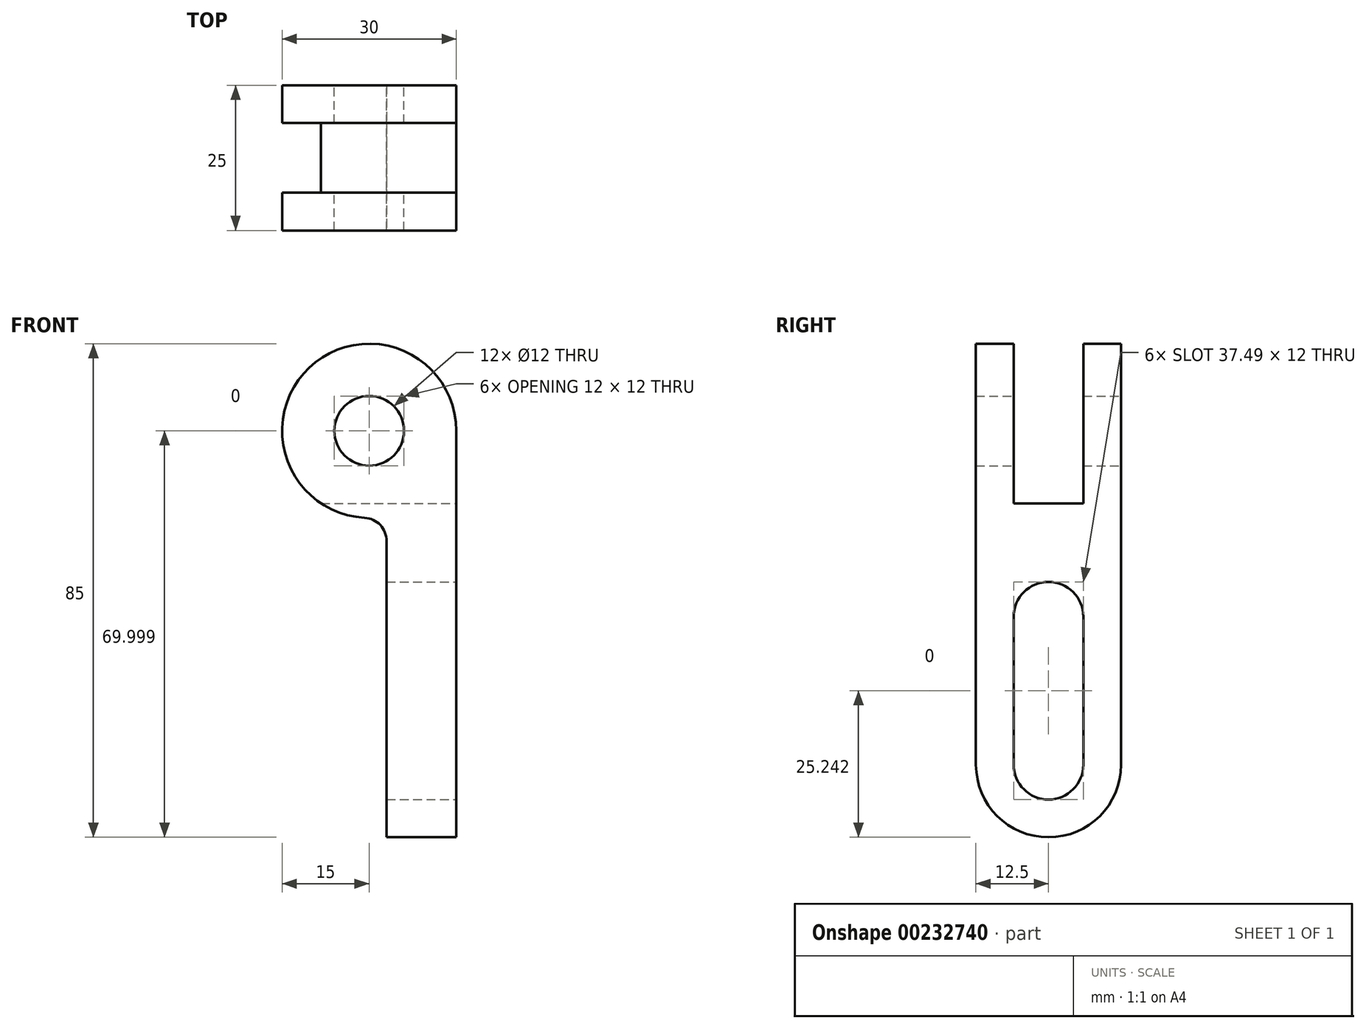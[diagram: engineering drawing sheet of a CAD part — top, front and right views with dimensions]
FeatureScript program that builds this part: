
annotation { "Feature Type Name" : "Feature", "Feature Type Description" : "" }
export const myFeature = defineFeature(function(context is Context, id is Id, definition is map)
    precondition{}
    {
        {
            var Q0;
            Q0=qCreatedBy(makeId("Front.planeOp"),FACE);
            var sketch = newSketch(context, id + "F0", { "sketchPlane" : qUnion([Q0])});
            skCircle(sketch, "E0", {"center": v(-31.82, 39.8) * mm, "radius": 6 * mm});
            skArc(sketch, "E1", {"start": v(-16.82, 39.8) * mm, "mid": v(-42.14, 50.7) * mm, "end": v(-32.6, 24.83) * mm});
            skLineSegment(sketch, "E2", {"start": v(-6.57, 39.8) * mm, "end": v(-62.09, 39.8) * mm, "construction": true});
            skLineSegment(sketch, "E3", {"start": v(-16.82, 39.8) * mm, "end": v(-16.82, -30.2) * mm});
            skLineSegment(sketch, "E4", {"start": v(-16.82, -30.2) * mm, "end": v(-28.82, -30.2) * mm});
            skLineSegment(sketch, "E5", {"start": v(-28.82, -30.2) * mm, "end": v(-28.82, 20.84) * mm});
            skArc(sketch, "E6", {"start": v(-28.82, 20.84) * mm, "mid": v(-29.92, 23.59) * mm, "end": v(-32.6, 24.83) * mm});
            skSolve(sketch);
        }
        {
            var Q0;
            Q0=makeQuery(id+"F0.imprint","IMPRINT",FACE,{"disambiguationData":[TD([[makeQuery(id+"F0.imprint","IMPRINT",EDGE,{"derivedFrom":sQuery(id+"F0.wireOp",EDGE,"E0")}),-1.0]])]});
            extrude(context, id + "F1", {"entities" : qUnion([Q0]), "depth" : 25 * mm});
        }
        {
            var Q0;
            Q0=qCreatedBy(makeId("Right.planeOp"),FACE);
            var sketch = newSketch(context, id + "F2", { "sketchPlane" : qUnion([Q0])});
            skLineSegment(sketch, "E7.0.1", {"start": v(0, -30.2) * mm, "end": v(-25, -30.2) * mm});
            skLineSegment(sketch, "E7.0.3", {"start": v(-25, 20.84) * mm, "end": v(0, 20.84) * mm});
            skLineSegment(sketch, "E8.0", {"start": v(-25, 24.83) * mm, "end": v(0, 24.83) * mm});
            skLineSegment(sketch, "E9", {"start": v(-46.82, 54.8) * mm, "end": v(-46.82, 54.8) * mm});
            skLineSegment(sketch, "E10.0", {"start": v(-25, -30.2) * mm, "end": v(0, -30.2) * mm});
            skLineSegment(sketch, "E10.1", {"start": v(0, 24.83) * mm, "end": v(0, 24.83) * mm});
            skLineSegment(sketch, "E10.2", {"start": v(-25, 24.83) * mm, "end": v(-25, 24.83) * mm});
            skLineSegment(sketch, "E10.4", {"start": v(0, 20.84) * mm, "end": v(0, 24.83) * mm});
            skLineSegment(sketch, "E10.7", {"start": v(0, 33.8) * mm, "end": v(0, 45.8) * mm});
            skLineSegment(sketch, "E10.8", {"start": v(-25, 33.8) * mm, "end": v(-25, 45.8) * mm});
            skLineSegment(sketch, "E10.10", {"start": v(-25, 20.84) * mm, "end": v(-25, 24.83) * mm});
            skLineSegment(sketch, "E10.11", {"start": v(-25, -30.2) * mm, "end": v(0, -30.2) * mm});
            skLineSegment(sketch, "E10.12", {"start": v(-16.82, 39.8) * mm, "end": v(-16.82, 39.8) * mm});
            skLineSegment(sketch, "E10.15", {"start": v(0, -30.2) * mm, "end": v(0, -30.2) * mm});
            skLineSegment(sketch, "E10.16", {"start": v(-25, -30.2) * mm, "end": v(-25, -30.2) * mm});
            skLineSegment(sketch, "E11", {"start": v(-25, 54.8) * mm, "end": v(0, 54.8) * mm});
            skLineSegment(sketch, "E12.0.0", {"start": v(0, 20.84) * mm, "end": v(0, -30.2) * mm});
            skLineSegment(sketch, "E12.0.2", {"start": v(-25, -30.2) * mm, "end": v(-25, 20.84) * mm});
            skArc(sketch, "E13", {"start": v(-25, -17.7) * mm, "mid": v(-12.5, -30.2) * mm, "end": v(0, -17.7) * mm});
            skArc(sketch, "E14", {"start": v(-18.5, -17.7) * mm, "mid": v(-12.5, -23.7) * mm, "end": v(-6.5, -17.7) * mm});
            skArc(sketch, "E15", {"start": v(-6.5, 7.8) * mm, "mid": v(-12.5, 13.8) * mm, "end": v(-18.5, 7.8) * mm});
            skLineSegment(sketch, "E16", {"start": v(-12.5, -36.92) * mm, "end": v(-12.5, -23.7) * mm});
            skPoint(sketch, "E16.endSnap0", {"position": v(-12.5, 24.83) * mm});
            skLineSegment(sketch, "E17", {"start": v(-18.5, 7.8) * mm, "end": v(-18.5, -17.7) * mm});
            skLineSegment(sketch, "E18", {"start": v(-6.5, 7.8) * mm, "end": v(-6.5, -17.7) * mm});
            skLineSegment(sketch, "E19.trimOffspring", {"start": v(-12.5, 13.8) * mm, "end": v(-12.5, 65.83) * mm});
            skLineSegment(sketch, "E20.bottom", {"start": v(-6.5, 27.3) * mm, "end": v(-18.5, 27.3) * mm});
            skLineSegment(sketch, "E20.top", {"start": v(-6.5, 82.3) * mm, "end": v(-18.5, 82.3) * mm});
            skLineSegment(sketch, "E20.left", {"start": v(-6.5, 27.3) * mm, "end": v(-6.5, 82.3) * mm});
            skLineSegment(sketch, "E20.right", {"start": v(-18.5, 27.3) * mm, "end": v(-18.5, 82.3) * mm});
            skPoint(sketch, "E20.middle", {"position": v(-12.5, 54.8) * mm});
            skLineSegment(sketch, "E21", {"start": v(-25, 54.8) * mm, "end": v(-25, 24.83) * mm});
            skLineSegment(sketch, "E22", {"start": v(0, 54.8) * mm, "end": v(0, 24.83) * mm});
            skSolve(sketch);
        }
        {
            var Q0;
            {var subQ3=sQuery(id+"F2.wireOp",EDGE,"E17");Q0=makeQuery(id+"F2.imprint","IMPRINT",FACE,{"disambiguationData":[TD([[makeQuery(id+"F2.imprint","IMPRINT",EDGE,{"derivedFrom":subQ3}),1.0]])]});}
            var Q1;
            {var subQ0=sQuery(id+"F2.wireOp",EDGE,"E7.0.1");var subQ1=sQuery(id+"F2.wireOp",EDGE,"E12.0.0");var subQ2=makeQuery(id+"F2.imprint","INTERSECT",VERTEX,{"derivedFrom":[subQ1,subQ0]});Q1=makeQuery(id+"F2.imprint","IMPRINT",FACE,{"disambiguationData":[TD([[makeQuery(id+"F2.imprint","IMPRINT",EDGE,{"disambiguationData":[TD([[subQ2,1.0]])],"derivedFrom":subQ1}),-1.0]])]});}
            var Q2;
            {var subQ0=sQuery(id+"F2.wireOp",EDGE,"E12.0.2");var subQ1=sQuery(id+"F2.wireOp",EDGE,"E7.0.1");var subQ2=makeQuery(id+"F2.imprint","INTERSECT",VERTEX,{"derivedFrom":[subQ1,subQ0]});Q2=makeQuery(id+"F2.imprint","IMPRINT",FACE,{"disambiguationData":[TD([[makeQuery(id+"F2.imprint","IMPRINT",EDGE,{"disambiguationData":[TD([[subQ2,-1.0]])],"derivedFrom":subQ0}),-1.0]])]});}
            var Q3;
            {var subQ0=sQuery(id+"F2.wireOp",EDGE,"E20.right");var subQ1=sQuery(id+"F2.wireOp",EDGE,"E11");var subQ2=makeQuery(id+"F2.imprint","INTERSECT",VERTEX,{"derivedFrom":[subQ1,subQ0]});Q3=makeQuery(id+"F2.imprint","IMPRINT",FACE,{"disambiguationData":[TD([[makeQuery(id+"F2.imprint","IMPRINT",EDGE,{"disambiguationData":[TD([[subQ2,-1.0]])],"derivedFrom":subQ1}),-1.0]])]});}
            var Q4;
            {var subQ0=sQuery(id+"F2.wireOp",EDGE,"E19.trimOffspring");var subQ1=sQuery(id+"F2.wireOp",EDGE,"E11");var subQ2=makeQuery(id+"F2.imprint","INTERSECT",VERTEX,{"derivedFrom":[subQ1,subQ0]});Q4=makeQuery(id+"F2.imprint","IMPRINT",FACE,{"disambiguationData":[TD([[makeQuery(id+"F2.imprint","IMPRINT",EDGE,{"disambiguationData":[TD([[subQ2,-1.0]])],"derivedFrom":subQ1}),-1.0]])]});}
            extrude(context, id + "F3", {"entities" : qUnion([Q0, Q1, Q2, Q3, Q4]), "operationType" : NewBodyOperationType.REMOVE, "endBound" : BoundingType.THROUGH_ALL, "oppositeDirection" : true, "depth" : 25 * mm});
        }
    });
